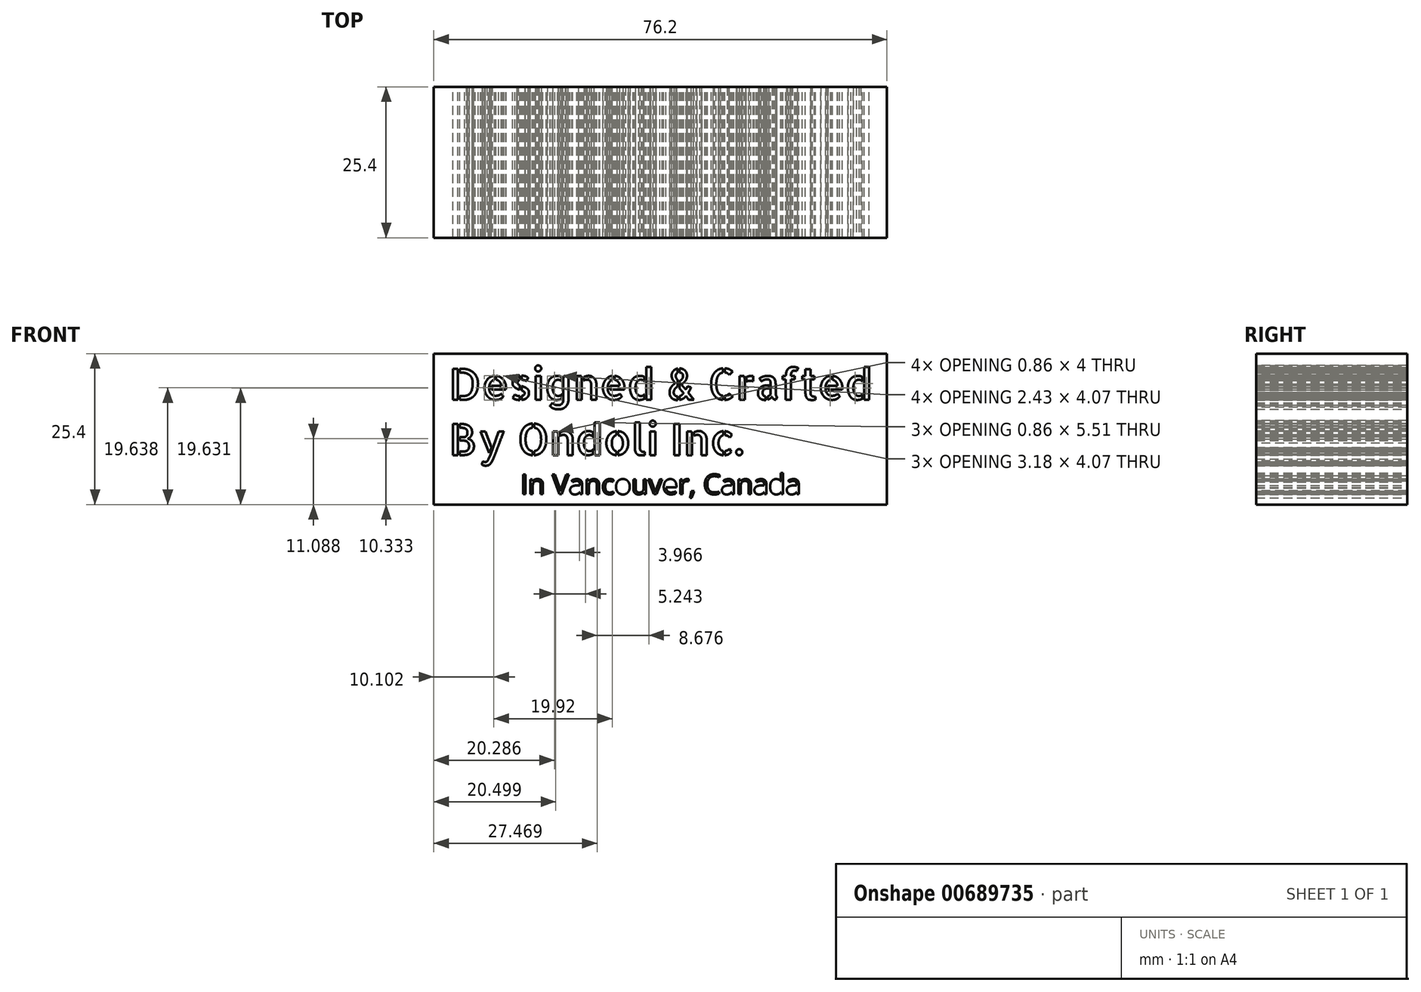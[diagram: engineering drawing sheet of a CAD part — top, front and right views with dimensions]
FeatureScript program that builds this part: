
annotation { "Feature Type Name" : "Feature", "Feature Type Description" : "" }
export const myFeature = defineFeature(function(context is Context, id is Id, definition is map)
    precondition{}
    {
        {
            var Q0;
            Q0=qCreatedBy(makeId("Front.planeOp"),FACE);
            var sketch = newSketch(context, id + "F0", { "sketchPlane" : qUnion([Q0])});
            skLineSegment(sketch, "E0.bottom", {"start": v(-38.1, 25.4) * mm, "end": v(38.1, 25.4) * mm});
            skLineSegment(sketch, "E0.top", {"start": v(-38.1, -25.4) * mm, "end": v(38.1, -25.4) * mm, "construction": true});
            skLineSegment(sketch, "E0.left", {"start": v(-38.1, 25.4) * mm, "end": v(-38.1, -25.4) * mm});
            skLineSegment(sketch, "E0.right", {"start": v(38.1, 25.4) * mm, "end": v(38.1, -25.4) * mm});
            skPoint(sketch, "E0.middle", {"position": v(0, 0) * mm});
            skText(sketch, "E1", { "text": "Designed & Crafted\nBy Ondoli Inc.", "fontName": "AllertaStencil-Regular.ttf"});
            skLineSegment(sketch, "E2", {"start": v(0, 0) * mm, "end": v(38.1, 0) * mm});
            skLineSegment(sketch, "E3", {"start": v(38.1, 0) * mm, "end": v(-38.1, 0) * mm});
            skText(sketch, "E4", { "text": "In Vancouver, Canada", "fontName": "OpenSans-Regular.ttf"});
            skLineSegment(sketch, "E5", {"start": v(0, 0) * mm, "end": v(0, 25.4) * mm, "construction": true});
            const initialGuessF0  = {"E1": [-0.03556, 0.01763, 1, 0, 0.00523], "E4": [-0.02355, 0.00175, 1, 0, 0.00336]};
            skSetInitialGuess(sketch, initialGuessF0);
            skSolve(sketch);
        }
        {
            var Q0;
            Q0 = qSketchRegion(id + "F0", true);
            extrude(context, id + "F1", {"entities" : qUnion([Q0]), "depth" : 25.4 * mm, "offsetDistance" : 25.4 * mm});
        }
    });
